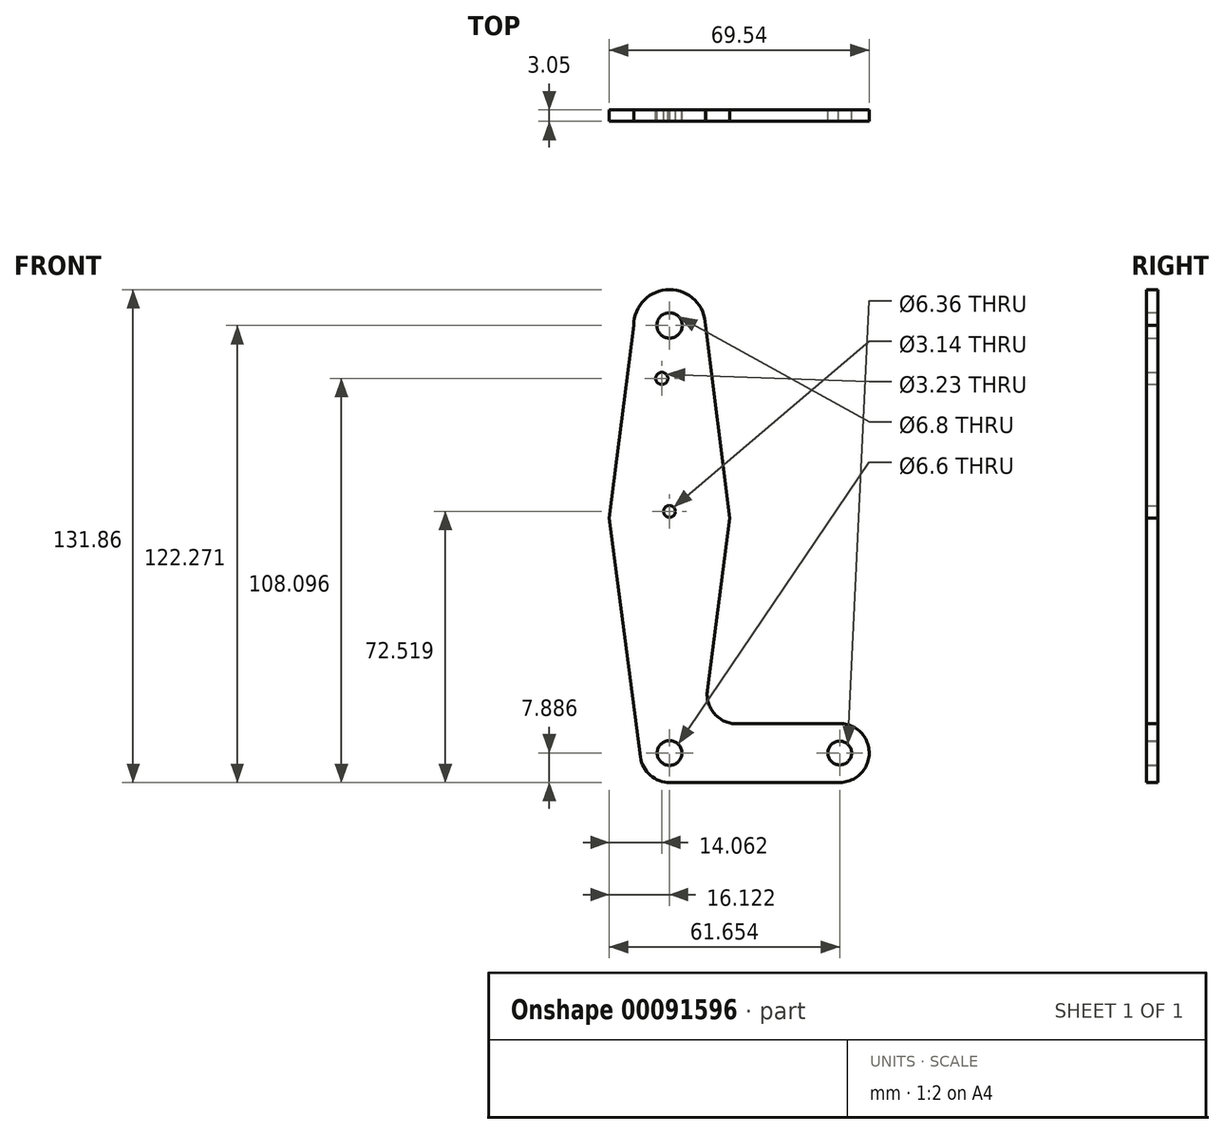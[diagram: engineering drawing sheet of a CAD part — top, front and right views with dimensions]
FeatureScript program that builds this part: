
annotation { "Feature Type Name" : "Feature", "Feature Type Description" : "" }
export const myFeature = defineFeature(function(context is Context, id is Id, definition is map)
    precondition{}
    {
        {
            var Q0;
            Q0=qCreatedBy(makeId("Front.planeOp"),FACE);
            var sketch = newSketch(context, id + "F0", { "sketchPlane" : qUnion([Q0])});
            skLineSegment(sketch, "E0", {"start": v(-53.75, 51.54) * mm, "end": v(-53.75, -62.84) * mm});
            skLineSegment(sketch, "E1", {"start": v(-53.75, -62.84) * mm, "end": v(-8.22, -62.84) * mm});
            skCircle(sketch, "E2", {"center": v(-53.75, 51.54) * mm, "radius": 9.6 * mm});
            skCircle(sketch, "E3", {"center": v(-8.22, -62.84) * mm, "radius": 7.88 * mm});
            skCircle(sketch, "E4", {"center": v(-53.75, -62.84) * mm, "radius": 7.88 * mm});
            skLineSegment(sketch, "E5", {"start": v(-53.75, -62.84) * mm, "end": v(-53.75, 1.79) * mm});
            skCircle(sketch, "E6", {"center": v(-53.75, 1.79) * mm, "radius": 15.77 * mm});
            skLineSegment(sketch, "E7", {"start": v(-44.16, 51.54) * mm, "end": v(-37.62, 0) * mm});
            skLineSegment(sketch, "E8", {"start": v(-63.34, 51.54) * mm, "end": v(-69.87, 0) * mm});
            skLineSegment(sketch, "E9", {"start": v(-69.87, 0) * mm, "end": v(-61.56, -63.86) * mm});
            skLineSegment(sketch, "E10", {"start": v(-37.62, 0) * mm, "end": v(-43.62, -46.08) * mm});
            skLineSegment(sketch, "E11", {"start": v(-35.7, -55.06) * mm, "end": v(-8.24, -54.96) * mm});
            skLineSegment(sketch, "E12", {"start": v(-53.87, -70.72) * mm, "end": v(-7.87, -70.72) * mm});
            skCircle(sketch, "E13", {"center": v(-53.75, 51.54) * mm, "radius": 3.4 * mm});
            skCircle(sketch, "E14", {"center": v(-53.75, 1.79) * mm, "radius": 1.57 * mm});
            skCircle(sketch, "E15", {"center": v(-8.22, -62.84) * mm, "radius": 3.18 * mm});
            skCircle(sketch, "E16", {"center": v(-53.75, -62.84) * mm, "radius": 3.3 * mm});
            skCircle(sketch, "E17", {"center": v(-55.8, 37.37) * mm, "radius": 1.62 * mm});
            skArc(sketch, "E18.filletArc", {"start": v(-43.62, -46.08) * mm, "mid": v(-41.7, -52.36) * mm, "end": v(-35.7, -55.06) * mm});
            skSolve(sketch);
        }
        {
            var Q0;
            Q0 = qSketchRegion(id + "F0", true);
            var Q1;
            {var subQ0=sQuery(id+"F0.wireOp",EDGE,"E16");var subQ1=sQuery(id+"F0.wireOp",EDGE,"E1");var subQ2=makeQuery(id+"F0.imprint","INTERSECT",VERTEX,{"derivedFrom":[subQ1,subQ0]});Q1=makeQuery(id+"F0.imprint","IMPRINT",FACE,{"disambiguationData":[TD([[makeQuery(id+"F0.imprint","IMPRINT",EDGE,{"disambiguationData":[TD([[subQ2,-1.0]])],"derivedFrom":subQ1}),1.0]])]});}
            extrude(context, id + "F1", {"entities" : qUnion([Q0, Q1]), "depth" : 3.05 * mm});
        }
    });
